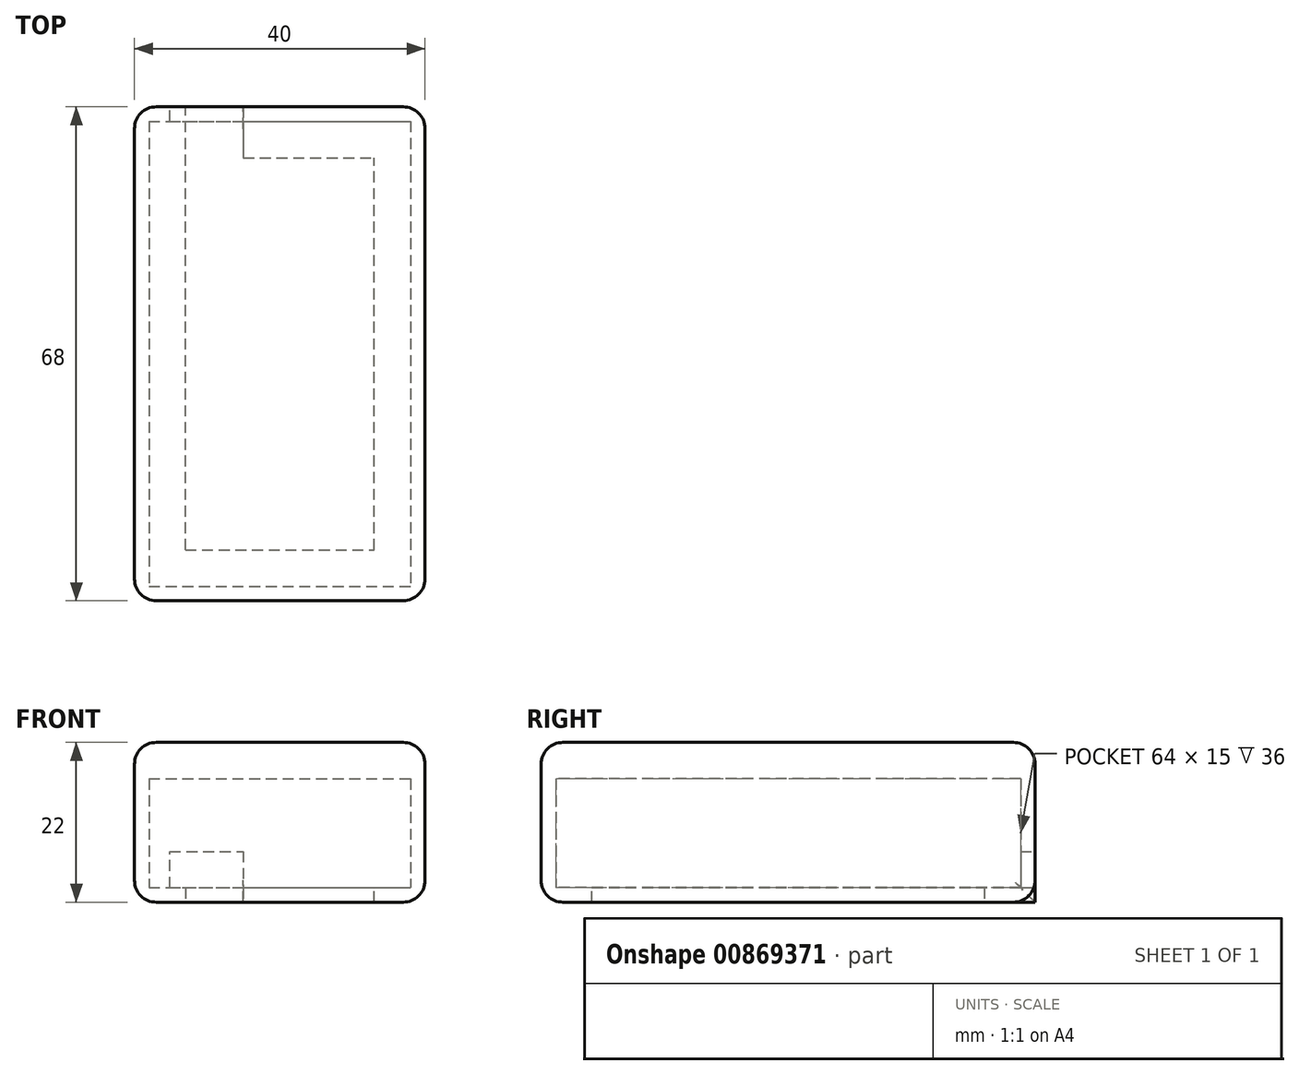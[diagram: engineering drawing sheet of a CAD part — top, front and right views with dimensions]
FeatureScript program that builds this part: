
annotation { "Feature Type Name" : "Feature", "Feature Type Description" : "" }
export const myFeature = defineFeature(function(context is Context, id is Id, definition is map)
    precondition{}
    {
        {
            var Q0;
            Q0=qCreatedBy(makeId("Top.planeOp"),FACE);
            var sketch = newSketch(context, id + "F0", { "sketchPlane" : qUnion([Q0])});
            skLineSegment(sketch, "E0.bottom", {"start": v(-20, 34) * mm, "end": v(20, 34) * mm});
            skLineSegment(sketch, "E0.top", {"start": v(-20, -34) * mm, "end": v(20, -34) * mm});
            skLineSegment(sketch, "E0.left", {"start": v(-20, 34) * mm, "end": v(-20, -34) * mm});
            skLineSegment(sketch, "E0.right", {"start": v(20, 34) * mm, "end": v(20, -34) * mm});
            skPoint(sketch, "E0.middle", {"position": v(0, 0) * mm});
            skLineSegment(sketch, "E1.0", {"start": v(-18, 32) * mm, "end": v(-18, -32) * mm});
            skLineSegment(sketch, "E1.1", {"start": v(-18, 32) * mm, "end": v(18, 32) * mm});
            skLineSegment(sketch, "E1.2", {"start": v(18, 32) * mm, "end": v(18, -32) * mm});
            skLineSegment(sketch, "E1.3", {"start": v(-18, -32) * mm, "end": v(18, -32) * mm});
            skSolve(sketch);
        }
        {
            var Q0;
            Q0=makeQuery(id+"F0.imprint","IMPRINT",FACE,{"disambiguationData":[TD([[makeQuery(id+"F0.imprint","IMPRINT",EDGE,{"derivedFrom":sQuery(id+"F0.wireOp",EDGE,"E0.bottom")}),-1.0]])]});
            var Q1;
            Q1=makeQuery(id+"F0.imprint","IMPRINT",FACE,{"disambiguationData":[TD([[makeQuery(id+"F0.imprint","IMPRINT",EDGE,{"derivedFrom":sQuery(id+"F0.wireOp",EDGE,"E1.0")}),1.0]])]});
            extrude(context, id + "F1", {"entities" : qUnion([Q0, Q1]), "depth" : 20 * mm, "offsetDistance" : 25 * mm});
        }
        {
            var Q0;
            Q0=makeQuery(id+"F0.imprint","IMPRINT",FACE,{"disambiguationData":[TD([[makeQuery(id+"F0.imprint","IMPRINT",EDGE,{"derivedFrom":sQuery(id+"F0.wireOp",EDGE,"E1.0")}),1.0]])]});
            extrude(context, id + "F2", {"entities" : qUnion([Q0]), "operationType" : NewBodyOperationType.REMOVE, "depth" : 15 * mm, "offsetDistance" : 25 * mm});
        }
        {
            var Q0;
            Q0=makeQuery(id+"F1.opExtrude","SWEPT_FACE",FACE,{"disambiguationData":[OSD([sQuery(id+"F0.wireOp",EDGE,"E0.bottom")])]});
            var sketch = newSketch(context, id + "F3", { "sketchPlane" : qUnion([Q0])});
            skLineSegment(sketch, "E2.bottom", {"start": v(15.15, 0) * mm, "end": v(5.15, 0) * mm});
            skLineSegment(sketch, "E2.top", {"start": v(15.15, 5) * mm, "end": v(5.15, 5) * mm});
            skLineSegment(sketch, "E2.left", {"start": v(15.15, 0) * mm, "end": v(15.15, 5) * mm});
            skLineSegment(sketch, "E2.right", {"start": v(5.15, 0) * mm, "end": v(5.15, 5) * mm});
            skSolve(sketch);
        }
        {
            var Q0;
            Q0=makeQuery(id+"F3.imprint","IMPRINT",FACE,{"disambiguationData":[TD([[makeQuery(id+"F3.imprint","IMPRINT",EDGE,{"derivedFrom":sQuery(id+"F3.wireOp",EDGE,"E2.bottom")}),-1.0]])]});
            extrude(context, id + "F4", {"entities" : qUnion([Q0]), "operationType" : NewBodyOperationType.REMOVE, "oppositeDirection" : true, "depth" : 25 * mm, "offsetDistance" : 25 * mm});
        }
        {
            var Q0;
            Q0=makeQuery(id+"F1.opExtrude","CAP_FACE",FACE,{"disambiguationData":[OSD([sQuery(id+"F0.wireOp",EDGE,"E0.bottom"),sQuery(id+"F0.wireOp",EDGE,"E0.top"),sQuery(id+"F0.wireOp",EDGE,"E0.left"),sQuery(id+"F0.wireOp",EDGE,"E0.right")])],"isStart":true});
            var sketch = newSketch(context, id + "F5", { "sketchPlane" : qUnion([Q0])});
            skLineSegment(sketch, "E3.bottom", {"start": v(-18, 32) * mm, "end": v(18, 32) * mm, "construction": true});
            skLineSegment(sketch, "E3.top", {"start": v(-18, -32) * mm, "end": v(18, -32) * mm, "construction": true});
            skLineSegment(sketch, "E3.left", {"start": v(-18, 32) * mm, "end": v(-18, -32) * mm, "construction": true});
            skLineSegment(sketch, "E3.right", {"start": v(18, 32) * mm, "end": v(18, -32) * mm, "construction": true});
            skLineSegment(sketch, "E4.0", {"start": v(-13, 27) * mm, "end": v(13, 27) * mm});
            skLineSegment(sketch, "E4.1", {"start": v(-13, 27) * mm, "end": v(-13, -27) * mm});
            skLineSegment(sketch, "E4.2", {"start": v(-13, -27) * mm, "end": v(13, -27) * mm});
            skLineSegment(sketch, "E4.3", {"start": v(13, 27) * mm, "end": v(13, -27) * mm});
            skLineSegment(sketch, "E5.bottom", {"start": v(-20, 34) * mm, "end": v(20, 34) * mm});
            skLineSegment(sketch, "E5.top", {"start": v(-20, -34) * mm, "end": v(20, -34) * mm});
            skLineSegment(sketch, "E5.left", {"start": v(-20, 34) * mm, "end": v(-20, -34) * mm});
            skLineSegment(sketch, "E5.right", {"start": v(20, 34) * mm, "end": v(20, -34) * mm});
            skSolve(sketch);
        }
        {
            var Q0;
            Q0=makeQuery(id+"F5.imprint","IMPRINT",FACE,{"disambiguationData":[TD([[makeQuery(id+"F5.imprint","IMPRINT",EDGE,{"derivedFrom":sQuery(id+"F5.wireOp",EDGE,"E5.bottom")}),-1.0]])]});
            var Q1;
            Q1=makeQuery(id+"F5.imprint","IMPRINT",FACE,{"disambiguationData":[TD([[makeQuery(id+"F5.imprint","IMPRINT",EDGE,{"derivedFrom":sQuery(id+"F5.wireOp",EDGE,"E4.0")}),1.0]])]});
            extrude(context, id + "F6", {"entities" : qUnion([Q0, Q1]), "operationType" : NewBodyOperationType.ADD, "depth" : 2 * mm, "offsetDistance" : 25 * mm});
        }
        {
            var Q0;
            Q0=makeQuery(id+"F6.opExtrude","CAP_FACE",FACE,{"disambiguationData":[OSD([sQuery(id+"F5.wireOp",EDGE,"E4.0"),sQuery(id+"F5.wireOp",EDGE,"E4.1"),sQuery(id+"F5.wireOp",EDGE,"E4.2"),sQuery(id+"F5.wireOp",EDGE,"E4.3"),sQuery(id+"F5.wireOp",EDGE,"E5.bottom"),sQuery(id+"F5.wireOp",EDGE,"E5.top"),sQuery(id+"F5.wireOp",EDGE,"E5.left"),sQuery(id+"F5.wireOp",EDGE,"E5.right")])],"isStart":false});
            var sketch = newSketch(context, id + "F7", { "sketchPlane" : qUnion([Q0])});
            skLineSegment(sketch, "E6.bottom", {"start": v(-5.03, -34) * mm, "end": v(-13, -34) * mm});
            skLineSegment(sketch, "E6.top", {"start": v(-5.03, -27) * mm, "end": v(-13, -27) * mm});
            skLineSegment(sketch, "E6.left", {"start": v(-5.03, -34) * mm, "end": v(-5.03, -27) * mm});
            skLineSegment(sketch, "E6.right", {"start": v(-13, -34) * mm, "end": v(-13, -27) * mm});
            skSolve(sketch);
        }
        {
            var Q0;
            Q0=makeQuery(id+"F7.imprint","IMPRINT",FACE,{"disambiguationData":[TD([[makeQuery(id+"F7.imprint","IMPRINT",EDGE,{"derivedFrom":sQuery(id+"F7.wireOp",EDGE,"E6.bottom")}),1.0]])]});
            extrude(context, id + "F8", {"entities" : qUnion([Q0]), "operationType" : NewBodyOperationType.REMOVE, "oppositeDirection" : true, "depth" : 7 * mm, "offsetDistance" : 25 * mm});
        }
        {
            var Q0;
            Q0=makeQuery(id+"F1.opExtrude","CAP_EDGE",EDGE,{"disambiguationData":[OSD([sQuery(id+"F0.wireOp",EDGE,"E0.left")])],"isStart":false});
            var Q1;
            Q1=makeQuery(id+"F1.opExtrude","CAP_EDGE",EDGE,{"disambiguationData":[OSD([sQuery(id+"F0.wireOp",EDGE,"E0.top")])],"isStart":false});
            var Q2;
            Q2=makeQuery(id+"F1.opExtrude","CAP_EDGE",EDGE,{"disambiguationData":[OSD([sQuery(id+"F0.wireOp",EDGE,"E0.right")])],"isStart":false});
            var Q3;
            Q3=makeQuery(id+"F1.opExtrude","CAP_EDGE",EDGE,{"disambiguationData":[OSD([sQuery(id+"F0.wireOp",EDGE,"E0.bottom")])],"isStart":false});
            var Q4;
            Q4=makeQuery(id+"F6.boolean.opBoolean","MERGE",EDGE,{"derivedFrom":[makeQuery(id+"F1.opExtrude","SWEPT_EDGE",EDGE,{"disambiguationData":[OSD([sQuery(id+"F0.wireOp",EDGE,"E0.bottom"),sQuery(id+"F0.wireOp",EDGE,"E0.right")])]}),makeQuery(id+"F6.opExtrude","SWEPT_EDGE",EDGE,{"disambiguationData":[OSD([sQuery(id+"F5.wireOp",EDGE,"E5.top"),sQuery(id+"F5.wireOp",EDGE,"E5.right")])]})]});
            var Q5;
            Q5=makeQuery(id+"F6.boolean.opBoolean","MERGE",FACE,{"derivedFrom":[makeQuery(id+"F1.opExtrude","SWEPT_FACE",FACE,{"disambiguationData":[OSD([sQuery(id+"F0.wireOp",EDGE,"E0.left")])]}),makeQuery(id+"F6.opExtrude","SWEPT_FACE",FACE,{"disambiguationData":[OSD([sQuery(id+"F5.wireOp",EDGE,"E5.left")])]})]});
            var Q6;
            Q6=makeQuery(id+"F6.boolean.opBoolean","MERGE",FACE,{"derivedFrom":[makeQuery(id+"F1.opExtrude","SWEPT_FACE",FACE,{"disambiguationData":[OSD([sQuery(id+"F0.wireOp",EDGE,"E0.right")])]}),makeQuery(id+"F6.opExtrude","SWEPT_FACE",FACE,{"disambiguationData":[OSD([sQuery(id+"F5.wireOp",EDGE,"E5.right")])]})]});
            var Q7;
            Q7=makeQuery(id+"F6.boolean.opBoolean","MERGE",FACE,{"derivedFrom":[makeQuery(id+"F1.opExtrude","SWEPT_FACE",FACE,{"disambiguationData":[OSD([sQuery(id+"F0.wireOp",EDGE,"E0.top")])]}),makeQuery(id+"F6.opExtrude","SWEPT_FACE",FACE,{"disambiguationData":[OSD([sQuery(id+"F5.wireOp",EDGE,"E5.bottom")])]})]});
            var Q8;
            {var subQ0=sQuery(id+"F5.wireOp",EDGE,"E5.top");Q8=makeQuery(id+"F8.boolean.opBoolean","SPLIT",EDGE,{"disambiguationData":[TD([makeQuery(id+"F1.opExtrude","SWEPT_FACE",FACE,{"disambiguationData":[OSD([sQuery(id+"F0.wireOp",EDGE,"E0.right")])]})])],"derivedFrom":makeQuery(id+"F6.opExtrude","CAP_EDGE",EDGE,{"disambiguationData":[OSD([subQ0])],"isStart":false})});}
            fillet(context, id + "F9", {"entities" : qUnion([Q0, Q1, Q2, Q3, Q4, Q5, Q6, Q7, Q8]), "radius" : 3 * mm, "tangentPropagation" : true, "allowEdgeOverflow" : false});
        }
    });
